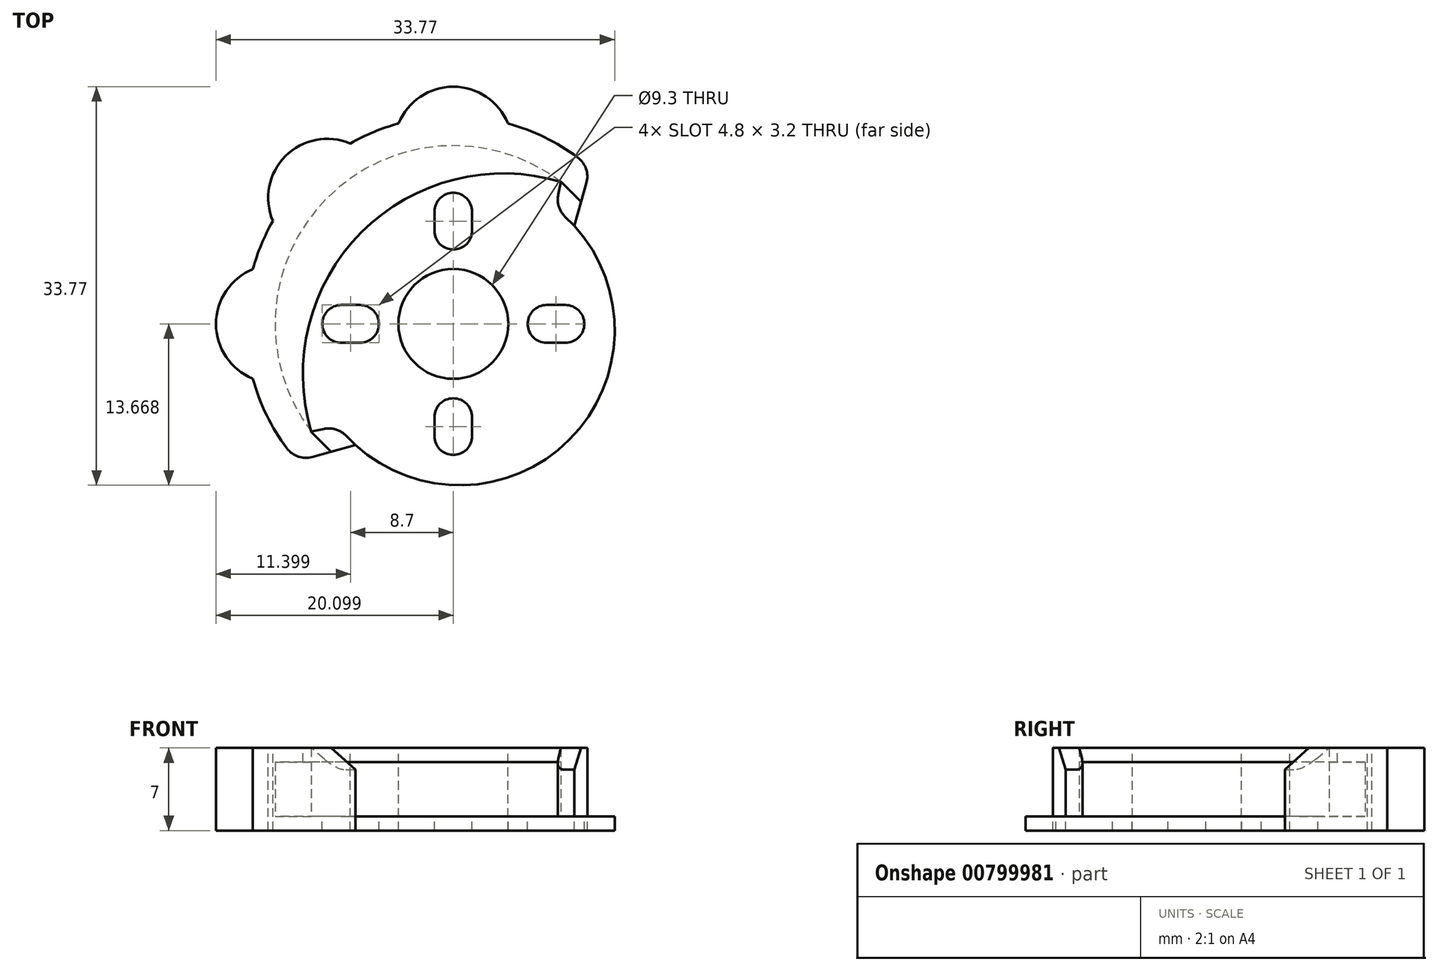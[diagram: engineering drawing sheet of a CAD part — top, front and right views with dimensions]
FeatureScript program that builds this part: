
annotation { "Feature Type Name" : "Feature", "Feature Type Description" : "" }
export const myFeature = defineFeature(function(context is Context, id is Id, definition is map)
    precondition{}
    {
        {
            var Q0;
            Q0=qCreatedBy(makeId("Top.planeOp"),FACE);
            var sketch = newSketch(context, id + "F0", { "sketchPlane" : qUnion([Q0])});
            skLineSegment(sketch, "E0.bottom", {"start": v(-22, 39) * mm, "end": v(22, 39) * mm});
            skLineSegment(sketch, "E0.top", {"start": v(-22, -39) * mm, "end": v(22, -39) * mm});
            skLineSegment(sketch, "E0.left", {"start": v(-22, 39) * mm, "end": v(-22, -39) * mm});
            skLineSegment(sketch, "E0.right", {"start": v(22, 39) * mm, "end": v(22, -39) * mm});
            skPoint(sketch, "E0.middle", {"position": v(0, 0) * mm});
            skArc(sketch, "E1", {"start": v(-64.94, 86.78) * mm, "mid": v(-84.74, 85.41) * mm, "end": v(-86.1, 65.62) * mm});
            skLineSegment(sketch, "E2", {"start": v(-83.94, 66.06) * mm, "end": v(-86.1, 65.62) * mm});
            skLineSegment(sketch, "E3", {"start": v(-74.06, 74.74) * mm, "end": v(-64.56, 74.74) * mm, "construction": true});
            skLineSegment(sketch, "E4", {"start": v(-74.06, 74.74) * mm, "end": v(-74.06, 84.24) * mm, "construction": true});
            skLineSegment(sketch, "E5", {"start": v(-74.06, 74.74) * mm, "end": v(-74.06, 65.24) * mm, "construction": true});
            skArc(sketch, "E6.3", {"start": v(-62.43, 87.95) * mm, "mid": v(-65.71, 90.23) * mm, "end": v(-69.43, 91.72) * mm});
            skLineSegment(sketch, "E6.4", {"start": v(-82.36, 64.48) * mm, "end": v(-87.27, 63.1) * mm});
            skLineSegment(sketch, "E7", {"start": v(-86.1, 65.62) * mm, "end": v(-87.27, 63.1) * mm});
            skLineSegment(sketch, "E8", {"start": v(-74.06, 74.74) * mm, "end": v(-64.24, 64.92) * mm, "construction": true});
            skLineSegment(sketch, "E9", {"start": v(-64.24, 64.92) * mm, "end": v(-46, 46.68) * mm, "construction": true});
            skLineSegment(sketch, "E10", {"start": v(-74.06, 74.74) * mm, "end": v(-83.56, 74.74) * mm, "construction": true});
            skLineSegment(sketch, "E11", {"start": v(-83.94, 66.06) * mm, "end": v(-82.36, 64.48) * mm});
            skLineSegment(sketch, "E12.MirrorCS", {"start": v(-65.39, 84.62) * mm, "end": v(-63.8, 83.04) * mm});
            skLineSegment(sketch, "E13.MirrorCS", {"start": v(-65.39, 84.62) * mm, "end": v(-64.94, 86.78) * mm});
            skLineSegment(sketch, "E14.MirrorCS", {"start": v(-63.8, 83.04) * mm, "end": v(-62.43, 87.95) * mm});
            skLineSegment(sketch, "E15.MirrorCS", {"start": v(-64.94, 86.78) * mm, "end": v(-62.43, 87.95) * mm});
            skCircle(sketch, "E16", {"center": v(-74.06, 74.74) * mm, "radius": 4.65 * mm});
            skArc(sketch, "E17", {"start": v(-72.46, 84.24) * mm, "mid": v(-74.06, 85.84) * mm, "end": v(-75.66, 84.24) * mm});
            skArc(sketch, "E18", {"start": v(-75.66, 82.64) * mm, "mid": v(-74.06, 81.04) * mm, "end": v(-72.46, 82.64) * mm});
            skLineSegment(sketch, "E19", {"start": v(-72.46, 84.24) * mm, "end": v(-72.46, 82.64) * mm});
            skLineSegment(sketch, "E20.MirrorCS", {"start": v(-75.66, 84.24) * mm, "end": v(-75.66, 82.64) * mm});
            skArc(sketch, "E21.1.0", {"start": v(-81.96, 73.14) * mm, "mid": v(-80.36, 74.74) * mm, "end": v(-81.96, 76.34) * mm});
            skLineSegment(sketch, "E21.1.1", {"start": v(-83.56, 73.14) * mm, "end": v(-81.96, 73.14) * mm});
            skLineSegment(sketch, "E21.1.2", {"start": v(-83.56, 76.34) * mm, "end": v(-81.96, 76.34) * mm});
            skArc(sketch, "E21.1.3", {"start": v(-83.56, 76.34) * mm, "mid": v(-85.16, 74.74) * mm, "end": v(-83.56, 73.14) * mm});
            skArc(sketch, "E21.2.0", {"start": v(-72.46, 66.84) * mm, "mid": v(-74.06, 68.44) * mm, "end": v(-75.66, 66.84) * mm});
            skLineSegment(sketch, "E21.2.1", {"start": v(-72.46, 65.24) * mm, "end": v(-72.46, 66.84) * mm});
            skLineSegment(sketch, "E21.2.2", {"start": v(-75.66, 65.24) * mm, "end": v(-75.66, 66.84) * mm});
            skArc(sketch, "E21.2.3", {"start": v(-75.66, 65.24) * mm, "mid": v(-74.06, 63.64) * mm, "end": v(-72.46, 65.24) * mm});
            skArc(sketch, "E21.3.0", {"start": v(-66.16, 76.34) * mm, "mid": v(-67.76, 74.74) * mm, "end": v(-66.16, 73.14) * mm});
            skLineSegment(sketch, "E21.3.1", {"start": v(-64.56, 76.34) * mm, "end": v(-66.16, 76.34) * mm});
            skLineSegment(sketch, "E21.3.2", {"start": v(-64.56, 73.14) * mm, "end": v(-66.16, 73.14) * mm});
            skArc(sketch, "E21.3.3", {"start": v(-64.56, 73.14) * mm, "mid": v(-62.96, 74.74) * mm, "end": v(-64.56, 76.34) * mm});
            skPoint(sketch, "E22.orphan", {"position": v(-80.08, 62.18) * mm});
            skPoint(sketch, "E23.orphan", {"position": v(-61.5, 80.75) * mm});
            skArc(sketch, "E24", {"start": v(-82.36, 64.48) * mm, "mid": v(-64.24, 64.92) * mm, "end": v(-63.8, 83.04) * mm});
            skLineSegment(sketch, "E25", {"start": v(-74.06, 74.74) * mm, "end": v(-59.56, 89.23) * mm, "construction": true});
            skArc(sketch, "E26", {"start": v(-69.43, 91.72) * mm, "mid": v(-74.06, 94.84) * mm, "end": v(-78.7, 91.72) * mm});
            skLineSegment(sketch, "E27", {"start": v(-74.06, 84.24) * mm, "end": v(-74.06, 94.85) * mm, "construction": true});
            skLineSegment(sketch, "E28", {"start": v(-83.56, 74.74) * mm, "end": v(-99.44, 74.74) * mm, "construction": true});
            skArc(sketch, "E29.1.0", {"start": v(-82.8, 90.02) * mm, "mid": v(-88.27, 88.95) * mm, "end": v(-89.34, 83.47) * mm});
            skArc(sketch, "E29.2.0", {"start": v(-91.04, 79.37) * mm, "mid": v(-94.16, 74.74) * mm, "end": v(-91.04, 70.1) * mm});
            skLineSegment(sketch, "E29.anchor1", {"start": v(-74.06, 74.74) * mm, "end": v(-78.7, 91.72) * mm, "construction": true});
            skLineSegment(sketch, "E29.anchor2", {"start": v(-74.06, 74.74) * mm, "end": v(-91.04, 70.1) * mm, "construction": true});
            skArc(sketch, "E30.trimOffspring", {"start": v(-78.7, 91.72) * mm, "mid": v(-80.8, 91) * mm, "end": v(-82.8, 90.02) * mm});
            skArc(sketch, "E31.trimOffspring", {"start": v(-89.34, 83.47) * mm, "mid": v(-90.32, 81.47) * mm, "end": v(-91.04, 79.37) * mm});
            skArc(sketch, "E32.trimOffspring", {"start": v(-91.04, 70.1) * mm, "mid": v(-89.56, 66.4) * mm, "end": v(-87.27, 63.1) * mm});
            skSolve(sketch);
        }
        {
            var Q0;
            Q0=makeQuery(id+"F0.imprint","IMPRINT",FACE,{"disambiguationData":[TD([[makeQuery(id+"F0.imprint","IMPRINT",EDGE,{"derivedFrom":sQuery(id+"F0.wireOp",EDGE,"E1")}),1.0]])]});
            var Q1;
            Q1=makeQuery(id+"F0.imprint","IMPRINT",FACE,{"disambiguationData":[TD([[makeQuery(id+"F0.imprint","IMPRINT",EDGE,{"derivedFrom":sQuery(id+"F0.wireOp",EDGE,"E1")}),-1.0]])]});
            var Q2;
            Q2=makeQuery(id+"F0.imprint","IMPRINT",FACE,{"disambiguationData":[TD([[makeQuery(id+"F0.imprint","IMPRINT",EDGE,{"derivedFrom":sQuery(id+"F0.wireOp",EDGE,"E2")}),1.0]])]});
            var Q3;
            Q3=makeQuery(id+"F0.imprint","IMPRINT",FACE,{"disambiguationData":[TD([[makeQuery(id+"F0.imprint","IMPRINT",EDGE,{"derivedFrom":sQuery(id+"F0.wireOp",EDGE,"E12.MirrorCS")}),1.0]])]});
            extrude(context, id + "F1", {"entities" : qUnion([Q0, Q1, Q2, Q3]), "oppositeDirection" : true, "depth" : 1.2 * mm, "offsetDistance" : 25 * mm});
        }
        {
            var Q0;
            Q0=makeQuery(id+"F0.imprint","IMPRINT",FACE,{"disambiguationData":[TD([[makeQuery(id+"F0.imprint","IMPRINT",EDGE,{"derivedFrom":sQuery(id+"F0.wireOp",EDGE,"E1")}),-1.0]])]});
            var Q1;
            Q1=makeQuery(id+"F0.imprint","IMPRINT",FACE,{"disambiguationData":[TD([[makeQuery(id+"F0.imprint","IMPRINT",EDGE,{"derivedFrom":sQuery(id+"F0.wireOp",EDGE,"E2")}),1.0]])]});
            var Q2;
            Q2=makeQuery(id+"F0.imprint","IMPRINT",FACE,{"disambiguationData":[TD([[makeQuery(id+"F0.imprint","IMPRINT",EDGE,{"derivedFrom":sQuery(id+"F0.wireOp",EDGE,"E12.MirrorCS")}),1.0]])]});
            extrude(context, id + "F2", {"entities" : qUnion([Q0, Q1, Q2]), "operationType" : NewBodyOperationType.ADD, "depth" : 5.8 * mm, "offsetDistance" : 25 * mm});
        }
        {
            var Q0;
            Q0=makeQuery(id+"F2.opExtrude","CAP_FACE",FACE,{"disambiguationData":[OSD([sQuery(id+"F0.wireOp",EDGE,"E1"),sQuery(id+"F0.wireOp",EDGE,"E6.3"),sQuery(id+"F0.wireOp",EDGE,"E7"),sQuery(id+"F0.wireOp",EDGE,"E15.MirrorCS"),sQuery(id+"F0.wireOp",EDGE,"E26"),sQuery(id+"F0.wireOp",EDGE,"E29.1.0"),sQuery(id+"F0.wireOp",EDGE,"E29.2.0"),sQuery(id+"F0.wireOp",EDGE,"E30.trimOffspring"),sQuery(id+"F0.wireOp",EDGE,"E31.trimOffspring"),sQuery(id+"F0.wireOp",EDGE,"E32.trimOffspring")])],"isStart":false});
            var sketch = newSketch(context, id + "F3", { "sketchPlane" : qUnion([Q0])});
            skArc(sketch, "E33.0", {"start": v(-64.94, 86.78) * mm, "mid": v(-84.74, 85.41) * mm, "end": v(-86.1, 65.62) * mm});
            skLineSegment(sketch, "E34.0", {"start": v(-63.8, 83.04) * mm, "end": v(-62.43, 87.95) * mm});
            skLineSegment(sketch, "E35.0", {"start": v(-82.36, 64.48) * mm, "end": v(-87.27, 63.1) * mm});
            skLineSegment(sketch, "E36.0", {"start": v(-86.1, 65.62) * mm, "end": v(-87.27, 63.1) * mm});
            skLineSegment(sketch, "E37.0", {"start": v(-64.94, 86.78) * mm, "end": v(-62.43, 87.95) * mm});
            skPoint(sketch, "E38", {"position": v(-74.06, 84.24) * mm});
            skPoint(sketch, "E39", {"position": v(-83.56, 74.74) * mm});
            skCircle(sketch, "E40", {"center": v(-74.06, 84.24) * mm, "radius": 2.5 * mm});
            skCircle(sketch, "E41", {"center": v(-83.56, 74.74) * mm, "radius": 2.5 * mm});
            skArc(sketch, "E42", {"start": v(-64.94, 86.78) * mm, "mid": v(-81.83, 82.5) * mm, "end": v(-86.1, 65.62) * mm});
            skSolve(sketch);
        }
        {
            var Q0;
            Q0=makeQuery(id+"F3.imprint","IMPRINT",FACE,{"disambiguationData":[TD([[makeQuery(id+"F3.imprint","IMPRINT",EDGE,{"derivedFrom":sQuery(id+"F3.wireOp",EDGE,"E33.0")}),1.0]])]});
            extrude(context, id + "F4", {"entities" : qUnion([Q0]), "operationType" : NewBodyOperationType.ADD, "oppositeDirection" : true, "depth" : 1.2 * mm, "offsetDistance" : 25 * mm});
        }
        {
            var Q0;
            Q0=makeQuery(id+"F2.opExtrude","CAP_EDGE",EDGE,{"disambiguationData":[OSD([sQuery(id+"F0.wireOp",EDGE,"E11")])],"isStart":false});
            var Q1;
            Q1=makeQuery(id+"F2.opExtrude","CAP_EDGE",EDGE,{"disambiguationData":[OSD([sQuery(id+"F0.wireOp",EDGE,"E12.MirrorCS")])],"isStart":false});
            chamfer(context, id + "F5", {"entities" : qUnion([Q0, Q1]), "width" : 1.85 * mm, "tangentPropagation" : true});
        }
        {
            var Q0;
            Q0=makeQuery(id+"F2.opExtrude","SWEPT_EDGE",EDGE,{"disambiguationData":[OSD([sQuery(id+"F0.wireOp",EDGE,"E2"),sQuery(id+"F0.wireOp",EDGE,"E11")])]});
            var Q1;
            Q1=makeQuery(id+"F2.opExtrude","SWEPT_EDGE",EDGE,{"disambiguationData":[OSD([sQuery(id+"F0.wireOp",EDGE,"E12.MirrorCS"),sQuery(id+"F0.wireOp",EDGE,"E13.MirrorCS")])]});
            var Q2;
            {var subQ0=sQuery(id+"F0.wireOp",EDGE,"E15.MirrorCS");var subQ1=sQuery(id+"F0.wireOp",EDGE,"E14.MirrorCS");var subQ2=sQuery(id+"F0.wireOp",EDGE,"E6.3");Q2=makeQuery(id+"F2.boolean.opBoolean","MERGE",EDGE,{"derivedFrom":[makeQuery(id+"F1.opExtrude","SWEPT_EDGE",EDGE,{"disambiguationData":[OSD([subQ2,subQ1,subQ0])]}),makeQuery(id+"F2.opExtrude","SWEPT_EDGE",EDGE,{"disambiguationData":[OSD([subQ2,subQ1,subQ0])]})]});}
            var Q3;
            {var subQ0=sQuery(id+"F0.wireOp",EDGE,"E32.trimOffspring");var subQ1=sQuery(id+"F0.wireOp",EDGE,"E7");var subQ2=sQuery(id+"F0.wireOp",EDGE,"E6.4");Q3=makeQuery(id+"F2.boolean.opBoolean","MERGE",EDGE,{"derivedFrom":[makeQuery(id+"F1.opExtrude","SWEPT_EDGE",EDGE,{"disambiguationData":[OSD([subQ2,subQ1,subQ0])]}),makeQuery(id+"F2.opExtrude","SWEPT_EDGE",EDGE,{"disambiguationData":[OSD([subQ2,subQ1,subQ0])]})]});}
            fillet(context, id + "F6", {"entities" : qUnion([Q0, Q1, Q2, Q3]), "tangentPropagation" : true, "radius" : 2 * mm, "defaultsChanged" : false, "vertexSettings" : [], "allowEdgeOverflow" : false});
        }
    });
